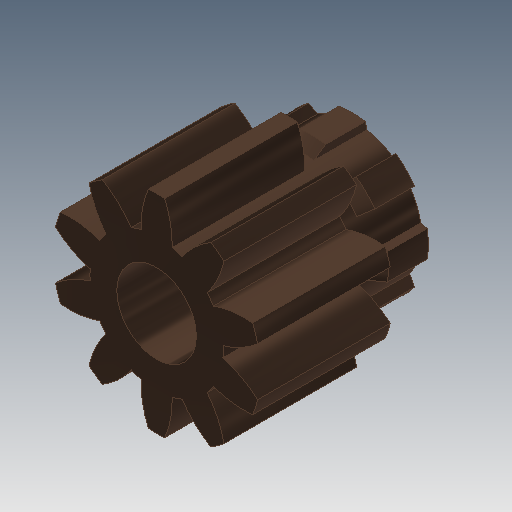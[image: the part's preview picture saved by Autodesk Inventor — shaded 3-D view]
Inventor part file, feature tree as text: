
AUTODESK INVENTOR PART (.ipt)
format: ipt  version: 2017 (Build 210142000, 142)  size: 263,680 bytes
history: native  units: mm (DEFAULTED — no unit token found)
features: sketch x5, extrude x4, plane x3, other x3, chamfer x2, pattern_circular x1
ambient origin geometry x8: Origin, YZ Plane, XZ Plane, XY Plane, X Axis, Y Axis, Z Axis, Center Point
bodies: Solid1 (feature_tree)
feature tree (18):
  extrude  "Extrusion1"  Depth=2.0mm TaperAngle=0.0deg
  plane  "Work Plane2"
  plane  "Work Plane8"
  plane  "Work Plane9"
  other  "Цилиндрическое зубчатое зацепление"
  extrude  "Выдавливание2"  Depth=10.0mm TaperAngle=0.0deg
  extrude  "Выдавливание3"  Depth=2.0mm
  chamfer  "Фаска1"  Distance=3.141593mm
  chamfer  "Фаска2"  [1 undecoded]
  pattern_circular  "Круговой массив1"  [2 undecoded]
  extrude  "Выдавливание4"  Depth=2.0mm
  sketch  "Sketch1"  dims[d0=3.135mm d1=2.0mm d2=0.0mm]
  sketch  "Sketch2"  dims[d3=2.5mm d4=10.0mm d5=0.0mm d16=6.0mm d17=0.0mm d34=3.141593mm d39=0.0mm d41=0.0mm d43=6.0mm d46=6.0mm d47=0.0mm d48=0.0mm d49=2.0mm d50=1.0mm d51=0.0mm d52=0.15mm d53=3.490659mm d54=0.8mm d55=0.0mm d56=0.15mm d57=2.0mm d58=45.0deg d59=0.15mm d60=0.05mm d61=45.0deg d62=80.0mm d63=360.0deg d65=1.2mm d66=5.2mm d67=0.0mm]
  other  "Srf1"
  sketch  "Эскиз3"
  sketch  "Эскиз4"
  sketch  "Эскиз5"
  other  "Средний диаметр"
note: 3 required parameter values undecoded (feature->parameter linkage not recoverable at this tier; creation-order binding heuristic only, values carry confidence <= 0.55)
